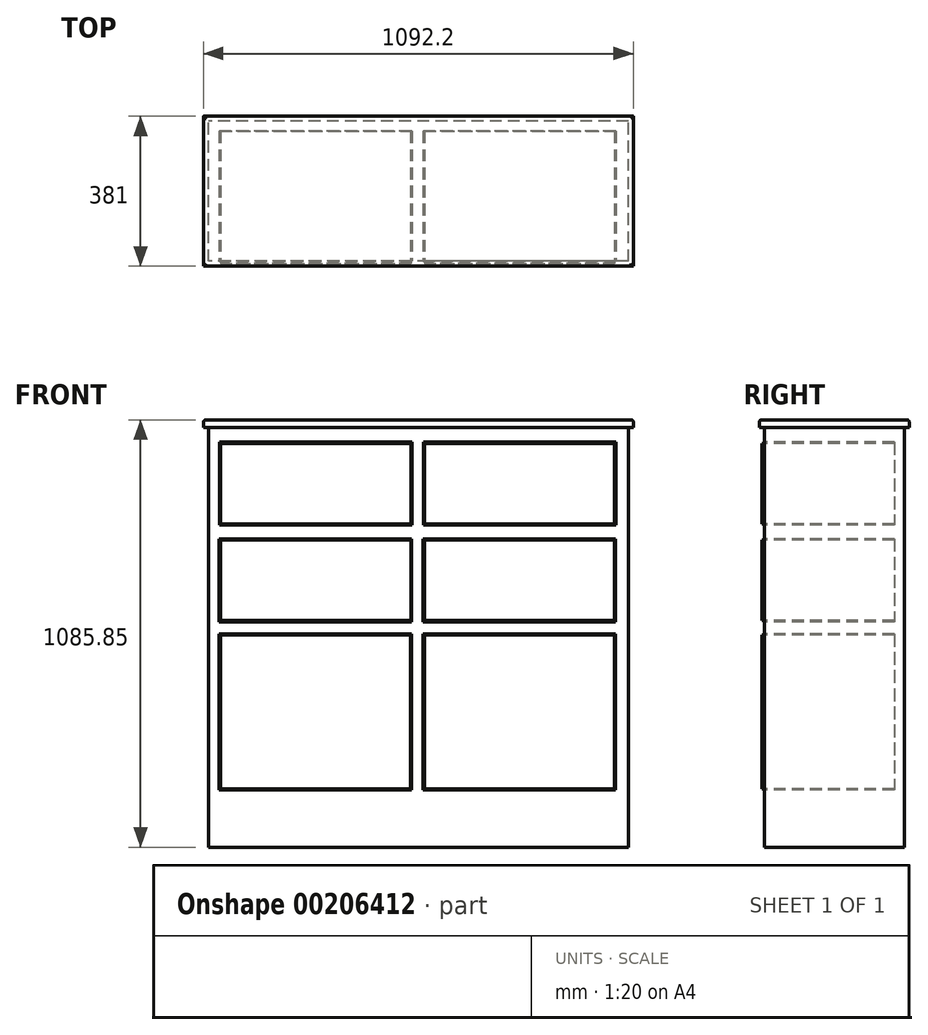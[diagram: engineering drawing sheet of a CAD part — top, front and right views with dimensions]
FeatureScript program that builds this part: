
annotation { "Feature Type Name" : "Feature", "Feature Type Description" : "" }
export const myFeature = defineFeature(function(context is Context, id is Id, definition is map)
    precondition{}
    {
        {
            var Q0;
            Q0=qCreatedBy(makeId("Front.planeOp"),FACE);
            var sketch = newSketch(context, id + "F0", { "sketchPlane" : qUnion([Q0])});
            skLineSegment(sketch, "E0.bottom", {"start": v(0, 0) * mm, "end": v(-1066.8, 0) * mm});
            skLineSegment(sketch, "E0.top", {"start": v(0, 1066.8) * mm, "end": v(-1066.8, 1066.8) * mm});
            skLineSegment(sketch, "E0.left", {"start": v(0, 0) * mm, "end": v(0, 1066.8) * mm});
            skLineSegment(sketch, "E0.right", {"start": v(-1066.8, 0) * mm, "end": v(-1066.8, 1066.8) * mm});
            skSolve(sketch);
        }
        {
            var Q0;
            Q0=makeQuery(id+"F0.imprint","IMPRINT",FACE,{"disambiguationData":[TD([[makeQuery(id+"F0.imprint","IMPRINT",EDGE,{"derivedFrom":sQuery(id+"F0.wireOp",EDGE,"E0.bottom")}),-1.0]])]});
            extrude(context, id + "F1", {"entities" : qUnion([Q0]), "depth" : 355.6 * mm});
        }
        {
            var Q0;
            Q0=makeQuery(id+"F1.opExtrude","SWEPT_FACE",FACE,{"disambiguationData":[OSD([sQuery(id+"F0.wireOp",EDGE,"E0.top")])]});
            var sketch = newSketch(context, id + "F2", { "sketchPlane" : qUnion([Q0])});
            skLineSegment(sketch, "E1.bottom", {"start": v(-1079.5, 12.7) * mm, "end": v(12.7, 12.7) * mm});
            skLineSegment(sketch, "E1.top", {"start": v(-1079.5, -368.3) * mm, "end": v(12.7, -368.3) * mm});
            skLineSegment(sketch, "E1.left", {"start": v(-1079.5, 12.7) * mm, "end": v(-1079.5, -368.3) * mm});
            skLineSegment(sketch, "E1.right", {"start": v(12.7, 12.7) * mm, "end": v(12.7, -368.3) * mm});
            skSolve(sketch);
        }
        {
            var Q0;
            Q0 = qSketchRegion(id + "F2", true);
            extrude(context, id + "F3", {"entities" : qUnion([Q0]), "operationType" : NewBodyOperationType.ADD, "depth" : 19.05 * mm});
        }
        {
            var Q0;
            Q0=makeQuery(id+"F3.opExtrude","CAP_FACE",FACE,{"disambiguationData":[OSD([sQuery(id+"F2.wireOp",EDGE,"E1.bottom"),sQuery(id+"F2.wireOp",EDGE,"E1.top"),sQuery(id+"F2.wireOp",EDGE,"E1.left"),sQuery(id+"F2.wireOp",EDGE,"E1.right")])],"isStart":false});
            fillet(context, id + "F4", {"entities" : qUnion([Q0]), "radius" : 6.35 * mm, "tangentPropagation" : true, "allowEdgeOverflow" : false});
        }
        {
            var Q0;
            Q0=makeQuery(id+"F1.opExtrude","CAP_FACE",FACE,{"disambiguationData":[OSD([sQuery(id+"F0.wireOp",EDGE,"E0.bottom"),sQuery(id+"F0.wireOp",EDGE,"E0.top"),sQuery(id+"F0.wireOp",EDGE,"E0.left"),sQuery(id+"F0.wireOp",EDGE,"E0.right")])],"isStart":false});
            var sketch = newSketch(context, id + "F5", { "sketchPlane" : qUnion([Q0])});
            skLineSegment(sketch, "E2.bottom", {"start": v(-549.4, 1029.28) * mm, "end": v(-1038.45, 1029.28) * mm});
            skLineSegment(sketch, "E2.top", {"start": v(-549.4, 818.5) * mm, "end": v(-1038.45, 818.5) * mm});
            skLineSegment(sketch, "E2.left", {"start": v(-549.4, 1029.28) * mm, "end": v(-549.4, 818.5) * mm});
            skLineSegment(sketch, "E2.right", {"start": v(-1038.45, 1029.28) * mm, "end": v(-1038.45, 818.5) * mm});
            skLineSegment(sketch, "E3.0.1.0", {"start": v(-550.32, 783.34) * mm, "end": v(-1039.37, 783.34) * mm});
            skLineSegment(sketch, "E3.0.1.1", {"start": v(-1039.37, 783.34) * mm, "end": v(-1039.37, 572.57) * mm});
            skLineSegment(sketch, "E3.0.1.2", {"start": v(-550.32, 572.57) * mm, "end": v(-1039.37, 572.57) * mm});
            skLineSegment(sketch, "E3.0.1.3", {"start": v(-550.32, 783.34) * mm, "end": v(-550.32, 572.57) * mm});
            skLineSegment(sketch, "E3.1.0.0", {"start": v(-31.24, 1029.28) * mm, "end": v(-520.3, 1029.28) * mm});
            skLineSegment(sketch, "E3.1.0.1", {"start": v(-520.3, 1029.28) * mm, "end": v(-520.3, 818.5) * mm});
            skLineSegment(sketch, "E3.1.0.2", {"start": v(-31.24, 818.5) * mm, "end": v(-520.3, 818.5) * mm});
            skLineSegment(sketch, "E3.1.0.3", {"start": v(-31.24, 1029.28) * mm, "end": v(-31.24, 818.5) * mm});
            skLineSegment(sketch, "E3.1.1.0", {"start": v(-32.16, 783.34) * mm, "end": v(-521.2, 783.34) * mm});
            skLineSegment(sketch, "E3.1.1.1", {"start": v(-521.2, 783.34) * mm, "end": v(-521.2, 572.57) * mm});
            skLineSegment(sketch, "E3.1.1.2", {"start": v(-32.16, 572.57) * mm, "end": v(-521.2, 572.57) * mm});
            skLineSegment(sketch, "E3.1.1.3", {"start": v(-32.16, 783.34) * mm, "end": v(-32.16, 572.57) * mm});
            skLineSegment(sketch, "E3.direction1", {"start": v(-1038.45, 1029.28) * mm, "end": v(-520.3, 1029.28) * mm, "construction": true});
            skLineSegment(sketch, "E3.direction2", {"start": v(-1038.45, 1029.28) * mm, "end": v(-1039.37, 783.34) * mm, "construction": true});
            skLineSegment(sketch, "E4.bottom", {"start": v(-1039.37, 541.87) * mm, "end": v(-550.32, 541.87) * mm});
            skLineSegment(sketch, "E4.top", {"start": v(-1039.37, 145.04) * mm, "end": v(-550.32, 145.04) * mm});
            skLineSegment(sketch, "E4.left", {"start": v(-1039.37, 541.87) * mm, "end": v(-1039.37, 145.04) * mm});
            skLineSegment(sketch, "E4.right", {"start": v(-550.32, 541.87) * mm, "end": v(-550.32, 145.04) * mm});
            skLineSegment(sketch, "E5.bottom", {"start": v(-521.2, 541.87) * mm, "end": v(-32.16, 541.87) * mm});
            skLineSegment(sketch, "E5.top", {"start": v(-521.2, 145.04) * mm, "end": v(-32.16, 145.04) * mm});
            skLineSegment(sketch, "E5.left", {"start": v(-521.2, 541.87) * mm, "end": v(-521.2, 145.04) * mm});
            skLineSegment(sketch, "E5.right", {"start": v(-32.16, 541.87) * mm, "end": v(-32.16, 145.04) * mm});
            skSolve(sketch);
        }
        {
            var Q0;
            Q0=makeQuery(id+"F5.imprint","IMPRINT",FACE,{"disambiguationData":[TD([[makeQuery(id+"F5.imprint","IMPRINT",EDGE,{"derivedFrom":sQuery(id+"F5.wireOp",EDGE,"E2.bottom")}),1.0]])]});
            var Q1;
            Q1=makeQuery(id+"F5.imprint","IMPRINT",FACE,{"disambiguationData":[TD([[makeQuery(id+"F5.imprint","IMPRINT",EDGE,{"derivedFrom":sQuery(id+"F5.wireOp",EDGE,"E3.1.0.0")}),1.0]])]});
            var Q2;
            Q2=makeQuery(id+"F5.imprint","IMPRINT",FACE,{"disambiguationData":[TD([[makeQuery(id+"F5.imprint","IMPRINT",EDGE,{"derivedFrom":sQuery(id+"F5.wireOp",EDGE,"E3.1.1.0")}),1.0]])]});
            var Q3;
            Q3=makeQuery(id+"F5.imprint","IMPRINT",FACE,{"disambiguationData":[TD([[makeQuery(id+"F5.imprint","IMPRINT",EDGE,{"derivedFrom":sQuery(id+"F5.wireOp",EDGE,"E3.0.1.0")}),1.0]])]});
            var Q4;
            Q4=makeQuery(id+"F5.imprint","IMPRINT",FACE,{"disambiguationData":[TD([[makeQuery(id+"F5.imprint","IMPRINT",EDGE,{"derivedFrom":sQuery(id+"F5.wireOp",EDGE,"E4.bottom")}),-1.0]])]});
            var Q5;
            Q5=makeQuery(id+"F5.imprint","IMPRINT",FACE,{"disambiguationData":[TD([[makeQuery(id+"F5.imprint","IMPRINT",EDGE,{"derivedFrom":sQuery(id+"F5.wireOp",EDGE,"E5.bottom")}),-1.0]])]});
            extrude(context, id + "F6", {"entities" : qUnion([Q0, Q1, Q2, Q3, Q4, Q5]), "operationType" : NewBodyOperationType.REMOVE, "oppositeDirection" : true, "depth" : 330.2 * mm});
        }
        {
            var Q0;
            Q0=makeQuery(id+"F1.opExtrude","CAP_FACE",FACE,{"disambiguationData":[OSD([sQuery(id+"F0.wireOp",EDGE,"E0.bottom"),sQuery(id+"F0.wireOp",EDGE,"E0.top"),sQuery(id+"F0.wireOp",EDGE,"E0.left"),sQuery(id+"F0.wireOp",EDGE,"E0.right")])],"isStart":false});
            var sketch = newSketch(context, id + "F7", { "sketchPlane" : qUnion([Q0])});
            skLineSegment(sketch, "E6.0", {"start": v(-552.48, 1026.2) * mm, "end": v(-1035.37, 1026.2) * mm});
            skLineSegment(sketch, "E6.1", {"start": v(-552.48, 1026.2) * mm, "end": v(-552.48, 821.59) * mm});
            skLineSegment(sketch, "E6.2", {"start": v(-552.48, 821.59) * mm, "end": v(-1035.37, 821.59) * mm});
            skLineSegment(sketch, "E6.3", {"start": v(-1035.37, 1026.2) * mm, "end": v(-1035.37, 821.59) * mm});
            skLineSegment(sketch, "E7.0.1.0", {"start": v(-552.48, 780.83) * mm, "end": v(-1035.37, 780.83) * mm});
            skLineSegment(sketch, "E7.0.1.1", {"start": v(-552.48, 780.83) * mm, "end": v(-552.48, 576.22) * mm});
            skLineSegment(sketch, "E7.0.1.2", {"start": v(-552.48, 576.22) * mm, "end": v(-1035.37, 576.22) * mm});
            skLineSegment(sketch, "E7.0.1.3", {"start": v(-1035.37, 780.83) * mm, "end": v(-1035.37, 576.22) * mm});
            skLineSegment(sketch, "E7.1.0.0", {"start": v(-34.63, 1026.2) * mm, "end": v(-517.52, 1026.2) * mm});
            skLineSegment(sketch, "E7.1.0.1", {"start": v(-34.63, 1026.2) * mm, "end": v(-34.63, 821.59) * mm});
            skLineSegment(sketch, "E7.1.0.2", {"start": v(-34.63, 821.59) * mm, "end": v(-517.52, 821.59) * mm});
            skLineSegment(sketch, "E7.1.0.3", {"start": v(-517.52, 1026.2) * mm, "end": v(-517.52, 821.59) * mm});
            skLineSegment(sketch, "E7.1.1.0", {"start": v(-34.63, 780.83) * mm, "end": v(-517.52, 780.83) * mm});
            skLineSegment(sketch, "E7.1.1.1", {"start": v(-34.63, 780.83) * mm, "end": v(-34.63, 576.22) * mm});
            skLineSegment(sketch, "E7.1.1.2", {"start": v(-34.63, 576.22) * mm, "end": v(-517.52, 576.22) * mm});
            skLineSegment(sketch, "E7.1.1.3", {"start": v(-517.52, 780.83) * mm, "end": v(-517.52, 576.22) * mm});
            skLineSegment(sketch, "E7.direction1", {"start": v(-1035.37, 1026.2) * mm, "end": v(-517.52, 1026.2) * mm, "construction": true});
            skLineSegment(sketch, "E7.direction2", {"start": v(-1035.37, 1026.2) * mm, "end": v(-1035.37, 780.83) * mm, "construction": true});
            skLineSegment(sketch, "E8.0", {"start": v(-1036.32, 538.83) * mm, "end": v(-553.37, 538.83) * mm});
            skLineSegment(sketch, "E8.1", {"start": v(-1036.32, 538.83) * mm, "end": v(-1036.32, 148.08) * mm});
            skLineSegment(sketch, "E8.2", {"start": v(-1036.32, 148.08) * mm, "end": v(-553.37, 148.08) * mm});
            skLineSegment(sketch, "E8.3", {"start": v(-553.37, 538.83) * mm, "end": v(-553.37, 148.08) * mm});
            skLineSegment(sketch, "E9.0", {"start": v(-518.16, 538.83) * mm, "end": v(-35.2, 538.83) * mm});
            skLineSegment(sketch, "E9.1", {"start": v(-518.16, 538.83) * mm, "end": v(-518.16, 148.08) * mm});
            skLineSegment(sketch, "E9.2", {"start": v(-518.16, 148.08) * mm, "end": v(-35.2, 148.08) * mm});
            skLineSegment(sketch, "E9.3", {"start": v(-35.2, 538.83) * mm, "end": v(-35.2, 148.08) * mm});
            skSolve(sketch);
        }
        {
            var Q0;
            Q0 = qSketchRegion(id + "F7", true);
            extrude(context, id + "F8", {"entities" : qUnion([Q0]), "operationType" : NewBodyOperationType.ADD, "oppositeDirection" : true, "depth" : 330.2 * mm, "hasSecondDirection" : true, "secondDirectionOppositeDirection" : false, "secondDirectionDepth" : 6.35 * mm});
        }
    });
